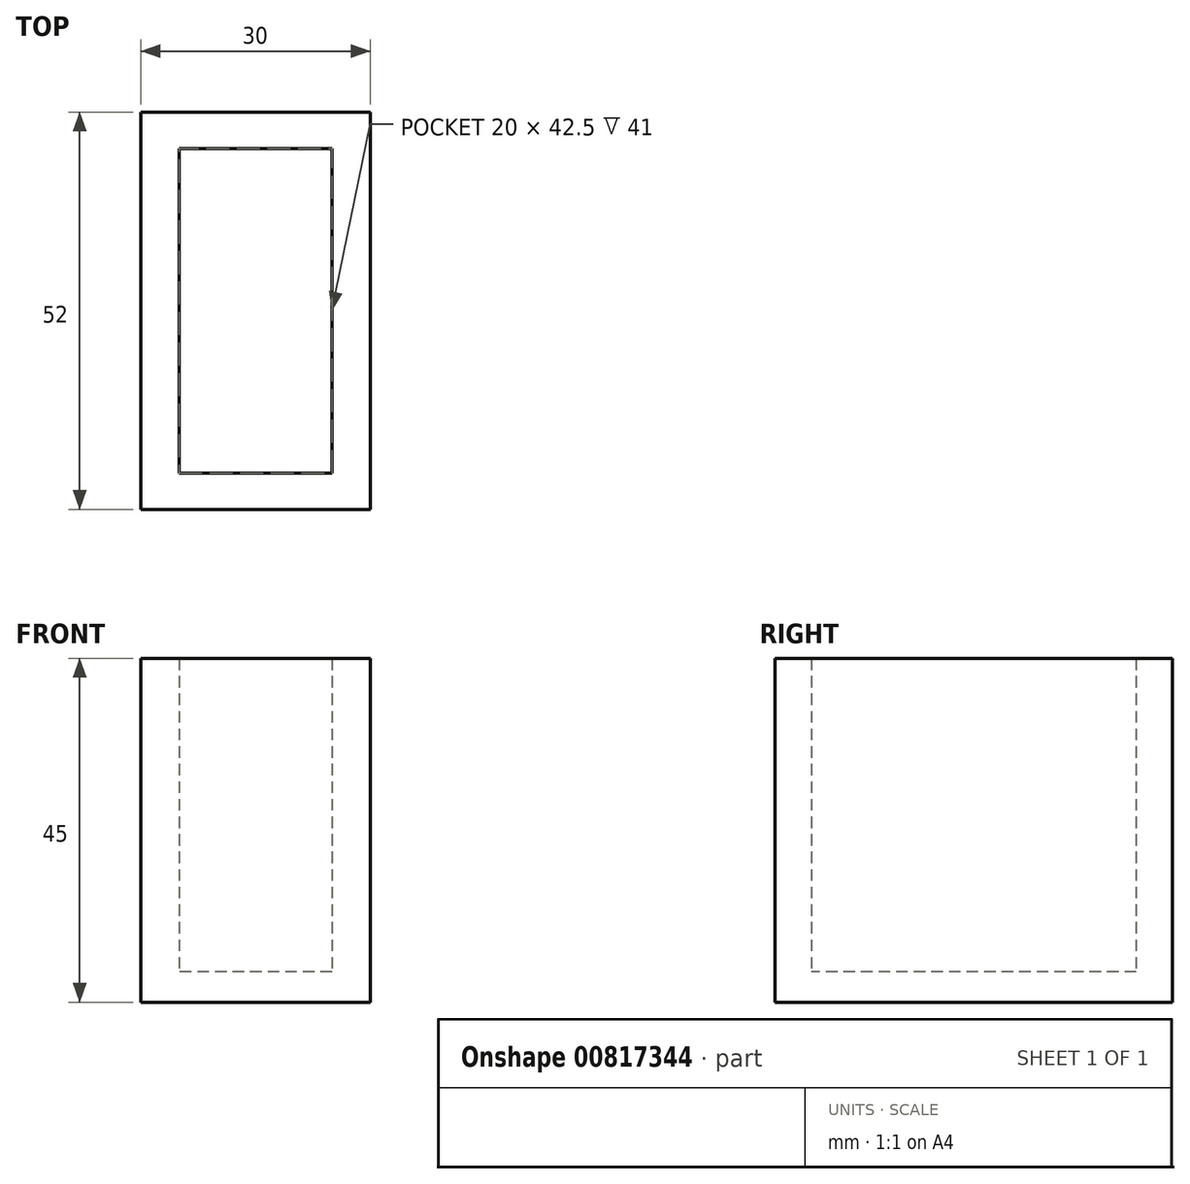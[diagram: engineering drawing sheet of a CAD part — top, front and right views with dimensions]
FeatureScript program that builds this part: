
annotation { "Feature Type Name" : "Feature", "Feature Type Description" : "" }
export const myFeature = defineFeature(function(context is Context, id is Id, definition is map)
    precondition{}
    {
        {
            var Q0;
            Q0=qCreatedBy(makeId("Top.planeOp"),FACE);
            var sketch = newSketch(context, id + "F0", { "sketchPlane" : qUnion([Q0])});
            skLineSegment(sketch, "E0.bottom", {"start": v(10, 21.25) * mm, "end": v(-10, 21.25) * mm});
            skLineSegment(sketch, "E0.top", {"start": v(10, -21.25) * mm, "end": v(-10, -21.25) * mm});
            skLineSegment(sketch, "E0.left", {"start": v(10, 21.25) * mm, "end": v(10, -21.25) * mm});
            skLineSegment(sketch, "E0.right", {"start": v(-10, 21.25) * mm, "end": v(-10, -21.25) * mm});
            skPoint(sketch, "E0.middle", {"position": v(0, 0) * mm});
            skLineSegment(sketch, "E1.bottom", {"start": v(15, 26) * mm, "end": v(-15, 26) * mm});
            skLineSegment(sketch, "E1.top", {"start": v(15, -26) * mm, "end": v(-15, -26) * mm});
            skLineSegment(sketch, "E1.left", {"start": v(15, 26) * mm, "end": v(15, -26) * mm});
            skLineSegment(sketch, "E1.right", {"start": v(-15, 26) * mm, "end": v(-15, -26) * mm});
            skSolve(sketch);
        }
        {
            var Q0;
            Q0 = qSketchRegion(id + "F0", true);
            extrude(context, id + "F1", {"entities" : qUnion([Q0]), "depth" : 41 * mm, "offsetDistance" : 25.4 * mm});
        }
        {
            var Q0;
            Q0=makeQuery(id+"F1.opExtrude","CAP_FACE",FACE,{"disambiguationData":[OSD([sQuery(id+"F0.wireOp",EDGE,"E0.bottom"),sQuery(id+"F0.wireOp",EDGE,"E0.top"),sQuery(id+"F0.wireOp",EDGE,"E0.left"),sQuery(id+"F0.wireOp",EDGE,"E0.right"),sQuery(id+"F0.wireOp",EDGE,"E1.bottom"),sQuery(id+"F0.wireOp",EDGE,"E1.top"),sQuery(id+"F0.wireOp",EDGE,"E1.left"),sQuery(id+"F0.wireOp",EDGE,"E1.right")])],"isStart":true});
            var sketch = newSketch(context, id + "F2", { "sketchPlane" : qUnion([Q0])});
            skLineSegment(sketch, "E2.bottom", {"start": v(15, 26) * mm, "end": v(-15, 26) * mm});
            skLineSegment(sketch, "E2.top", {"start": v(15, -26) * mm, "end": v(-15, -26) * mm});
            skLineSegment(sketch, "E2.left", {"start": v(15, 26) * mm, "end": v(15, -26) * mm});
            skLineSegment(sketch, "E2.right", {"start": v(-15, 26) * mm, "end": v(-15, -26) * mm});
            skPoint(sketch, "E2.middle", {"position": v(0, 0) * mm});
            skSolve(sketch);
        }
        {
            var Q0;
            Q0 = qSketchRegion(id + "F2", true);
            extrude(context, id + "F3", {"entities" : qUnion([Q0]), "operationType" : NewBodyOperationType.ADD, "depth" : 4 * mm, "offsetDistance" : 25.4 * mm});
        }
    });
